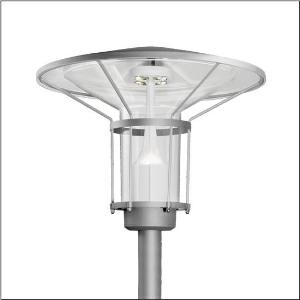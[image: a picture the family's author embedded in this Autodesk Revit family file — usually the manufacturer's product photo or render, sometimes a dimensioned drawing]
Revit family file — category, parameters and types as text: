
# Revit family: laterne_classic_iq___p1_0a_5xa5245bf14h_da05
name_source: partatom
category: Lighting Fixtures
units: mm (PartAtom-declared; Revit-internal decimal feet)

## family parameters
Cut with Voids When Loaded = No
Host = Face
Light Source = No
Part Type = Normal
Room Calculation Point = No
Round Connector Dimension = Use Diameter
Shared = No

## types (1)
- --- (1 x LED, 1360 lm, 12.9 W, 2200K)
    Apparent Load = 13 VA
    CIE Flux Codes = 30 61 91 96 100
    Color Rendering = 70
    Color Temperature = 2200K
    Default Elevation = 1800 mm
    Description = Lantern Classic iQ, mast luminaire, Module 540 iQ-SR, primary light control with 3 zone facetted reflector, of plastic, silver coated, highly specular, structured, primary optical cover: cover, of PMMA, transparent, light distribution: P1.0a, light emission: direct distribution, primary light characteristic: strongly asymmetric, installation type: post-top, LED, High Power LED, rated luminous flux: 1.360lm, luminous efficacy: 105lm/W, light colour: 722, colour temperature: 2200K, control gear: ECG iQ, control: pre-setting: logarithmic dimming characteristic, Street-Remote, Auto-Match, Temp-Guard, Lumen-Switch, Night-Set, Smart-Wire, Light-Fading, Desk-Remote (wireless, voltage-free reading and setting of iQ features in the workshop via application-optimized NFC function/RFID function), optimised constant luminous flux control (CLO 2.0), with terminal, 6-pole, max. 2.5mm², mains connection: 230..240V, AC, 50/60Hz, start of lifetime: 13W, end of service life: 13W, reduction: 6W, luminaire housing, upper part, of glass-fibre reinforced polyester, coated, Siteco® metallic grey (DB 702S), diameter: 750mm, height: 596mm, spigot size: d x l = 76 x 70mm (post-top) | with reducer (optional accessory) 60 x 70mm, post-top mast mounting element, of diecast aluminium, coated, Siteco® metallic grey (DB 702S), Module 540 iQ-SR, traffic white (RAL 9016), equipment: standard, protection rating (complete): IP65, insulation class (complete): insulation class II (safety insulation), certification: CE, ENEC, VDE, packaging unit: 1 piece

Light Distribution: P1.0a
    Height = 596 mm
    Lamp = 1 x LED
    Lamp Light Flux = 1360 lm
    Lamp Power = 12.9 W
    Lamp count = 1
    Length = 750 mm
    Luminous efficacy = 105 lm/W
    Manufacturer = Siteco
    ModVariant = No
    Model = 5XA5245BF14H
    Number of Poles = 1
    OnlyDefault = Yes
    Power Factor = 1
    Product Name = Laterne Classic iQ | P1.0a
    Product group = mast luminaire | pylon top
    ProductGroupID = 6100
    Protection Class = Protection class II
    Protection Degree = IP 65
    RLX_Detail_Level = 1
    RLX_Emergency_Light_Flux = 0 lm
    RLX_Emergency_Type = 0
    RLX_Emergency_Type_DB = No
    RlxData = <blob elided: 94193 chars, md5=25a1df58>
    Socket = socket
    Standby Power = 0 W
    System Light Flux = 1360 lm
    System Power = 13 W
    Type Comments = factory setting: luminous flux: 100 % | dim-lin: 254 | 516 mA
    Type Image = l_1006052.jpg
    URL = http://relux.com
    VarID = @adj_130635
    Voltage = 0 V
    Weight = 0.00 kg
    Width = 0 mm  [stored 0 ft]

note: [stored X ft] marks values corroborated as IEEE doubles in the binary element streams (Revit-internal decimal feet)

## geometry (parser evidence)
native form markers: Blend x4, Sweep x11
no freeform markers — native parametric forms only
